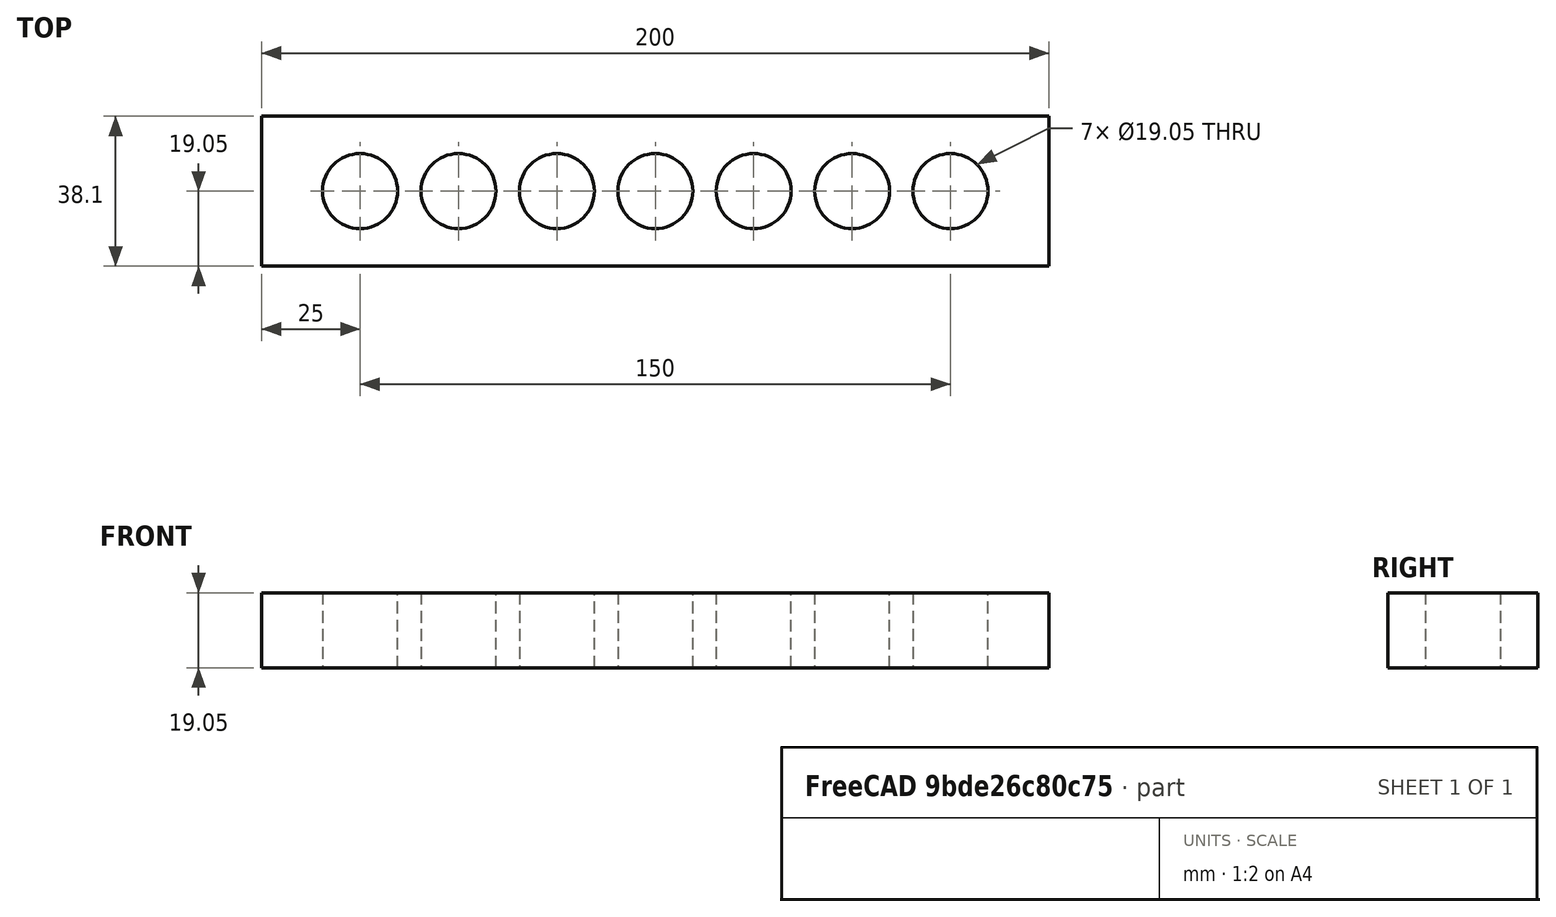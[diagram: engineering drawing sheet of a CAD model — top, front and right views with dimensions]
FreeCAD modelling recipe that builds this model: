
FCSTD DOCUMENT  (FreeCAD 0.19R24291 (Git))
Label: Base
License: All rights reserved
LicenseURL: http://en.wikipedia.org/wiki/All_rights_reserved
objects: TechDraw::DrawViewDimension×3, Sketcher::SketchObject×1, PartDesign::Pad×1, PartDesign::Body×1, TechDraw::DrawSVGTemplate×1, TechDraw::DrawViewPart×1, TechDraw::DrawPage×1
note: 4 computed .brp shape members not serialized (recipe doc carries the construction recipe); baked Part::Feature solids carry a one-line shape summary decoded from their .brp

FEATURE [Sketcher::SketchObject] Sketch001
  FullyConstrained = true
  MapMode = 5
  Support = -> [XY_Plane]
  expr: Constraints[15] = 3 / 4 * 25.4
  expr: Constraints[9] = 1.5 * 25.4
  sketch-geometry (12):
    g0: LineSegment StartX=0 StartY=0 StartZ=0 EndX=200 EndY=0 EndZ=0
    g1: LineSegment StartX=200 StartY=0 StartZ=0 EndX=200 EndY=38.1 EndZ=0
    g2: LineSegment StartX=200 StartY=38.1 StartZ=0 EndX=0 EndY=38.1 EndZ=0
    g3: LineSegment StartX=0 StartY=38.1 StartZ=0 EndX=0 EndY=0 EndZ=0
    g4: LineSegment StartX=0 StartY=19.05 StartZ=0 EndX=200 EndY=19.05 EndZ=0
    g5: Circle CenterX=25 CenterY=19.05 CenterZ=0 NormalX=0 NormalY=0 NormalZ=1 AngleXU=0 Radius=9.525
    g6: Circle CenterX=50 CenterY=19.05 CenterZ=0 NormalX=0 NormalY=0 NormalZ=1 AngleXU=0 Radius=9.525
    g7: Circle CenterX=75 CenterY=19.05 CenterZ=0 NormalX=0 NormalY=0 NormalZ=1 AngleXU=0 Radius=9.525
    g8: Circle CenterX=100 CenterY=19.05 CenterZ=0 NormalX=0 NormalY=0 NormalZ=1 AngleXU=0 Radius=9.525
    g9: Circle CenterX=125 CenterY=19.05 CenterZ=0 NormalX=0 NormalY=0 NormalZ=1 AngleXU=0 Radius=9.525
    g10: Circle CenterX=150 CenterY=19.05 CenterZ=0 NormalX=0 NormalY=0 NormalZ=1 AngleXU=0 Radius=9.525
    g11: Circle CenterX=175 CenterY=19.05 CenterZ=0 NormalX=0 NormalY=0 NormalZ=1 AngleXU=0 Radius=9.525
  constraints (35):
    c: Coincident(g0,g1)
    c: Coincident(g1,g2)
    c: Coincident(g2,g3)
    c: Coincident(g3,g0)
    c: Horizontal(g0)
    c: Horizontal(g2)
    c: Vertical(g1)
    c: Vertical(g3)
    c: Coincident(g0,g-1)
    c: DistanceY(g3,g3) = 38.1
    c: Symmetric(g0,g2,g4)
    c: Parallel(g4,g0)
    c: PointOnObject(g4,g1)
    c: PointOnObject(g5,g4)
    c: DistanceX(g4,g5) = 25
    c: Diameter(g5) = 19.05
    c: PointOnObject(g6,g4)
    c: DistanceX(g5,g6) = 25
    c: Equal(g6,g5)
    c: Equal(g5,g7) = 19.05
    c: PointOnObject(g7,g4)
    c: Equal(g5,g8) = 19.05
    c: PointOnObject(g8,g4)
    c: Equal(g5,g9) = 19.05
    c: PointOnObject(g9,g4)
    c: Equal(g5,g10) = 19.05
    c: PointOnObject(g10,g4)
    c: Equal(g5,g11) = 19.05
    c: PointOnObject(g11,g4)
    c: DistanceX(g6,g7) = 25
    c: DistanceX(g7,g8) = 25
    c: DistanceX(g8,g9) = 25
    c: DistanceX(g9,g10) = 25
    c: DistanceX(g10,g11) = 25
    c: DistanceX(g11,g4) = 25
FEATURE [PartDesign::Pad] Pad
  Direction = (1,1,1)
  Length = 19.05
  Length2 = 100
  Profile = -> Sketch001
  Type = 0
  expr: Length = 3 / 4 * 25.4
FEATURE [PartDesign::Body] Body
  Group = -> [Sketch001,Pad]
  Origin = -> Origin
  Tip = -> Pad
FEATURE [TechDraw::DrawSVGTemplate] Template
  EditableTexts = Designed_by_Name=Designed by Name; Drawing_number=Drawing number; FC-Date=Date; FC-SC=Scale; FC-SH=Sheet; FC-Title=Title; Subtitle=Subtitle; Weight=Weight
  Height = 210
  Orientation = 1
  Width = 297
FEATURE [TechDraw::DrawViewPart] View
  CoarseView = false
  Direction = (0,0,1)
  Focus = 100
  HardHidden = false
  IsoCount = 0
  IsoHidden = false
  IsoVisible = false
  LockPosition = false
  Perspective = false
  Rotation = 0
  ScaleType = 0
  SeamHidden = false
  SeamVisible = true
  SmoothHidden = false
  SmoothVisible = true
  Source = -> [Pad]
  X = 148.5
  XDirection = (-1,0,0)
  Y = 105
FEATURE [TechDraw::DrawViewDimension] Dimension
  Arbitrary = false
  ArbitraryTolerances = false
  EqualTolerance = true
  FormatSpec = %.2f
  FormatSpecOverTolerance = %+.2f
  FormatSpecUnderTolerance = %+.2f
  Inverted = false
  LockPosition = false
  MeasureType = 1
  OverTolerance = 0
  References2D = -> [View]
  Rotation = 0
  ScaleType = 0
  TheoreticalExact = false
  Type = 1
  UnderTolerance = 0
  X = -2.06219
  Y = 48.9518
FEATURE [TechDraw::DrawViewDimension] Dimension001
  Arbitrary = false
  ArbitraryTolerances = false
  EqualTolerance = true
  FormatSpec = %.2f
  FormatSpecOverTolerance = %+.2f
  FormatSpecUnderTolerance = %+.2f
  Inverted = false
  LockPosition = false
  MeasureType = 1
  OverTolerance = 0
  References2D = -> [View]
  Rotation = 0
  ScaleType = 0
  TheoreticalExact = false
  Type = 1
  UnderTolerance = 0
  X = -114.996
  Y = -25.7774
FEATURE [TechDraw::DrawViewDimension] Dimension002
  Arbitrary = false
  ArbitraryTolerances = false
  EqualTolerance = true
  FormatSpec = %.2f
  FormatSpecOverTolerance = %+.2f
  FormatSpecUnderTolerance = %+.2f
  Inverted = false
  LockPosition = false
  MeasureType = 1
  OverTolerance = 0
  References2D = -> [View]
  Rotation = 0
  ScaleType = 0
  TheoreticalExact = false
  Type = 1
  UnderTolerance = 0
  X = -118.306
  Y = -40.2128
FEATURE [TechDraw::DrawPage] Page
  KeepUpdated = true
  NextBalloonIndex = 1
  ProjectionType = 0
  Template = -> Template
  Views = -> [View,Dimension,Dimension001,Dimension002]
